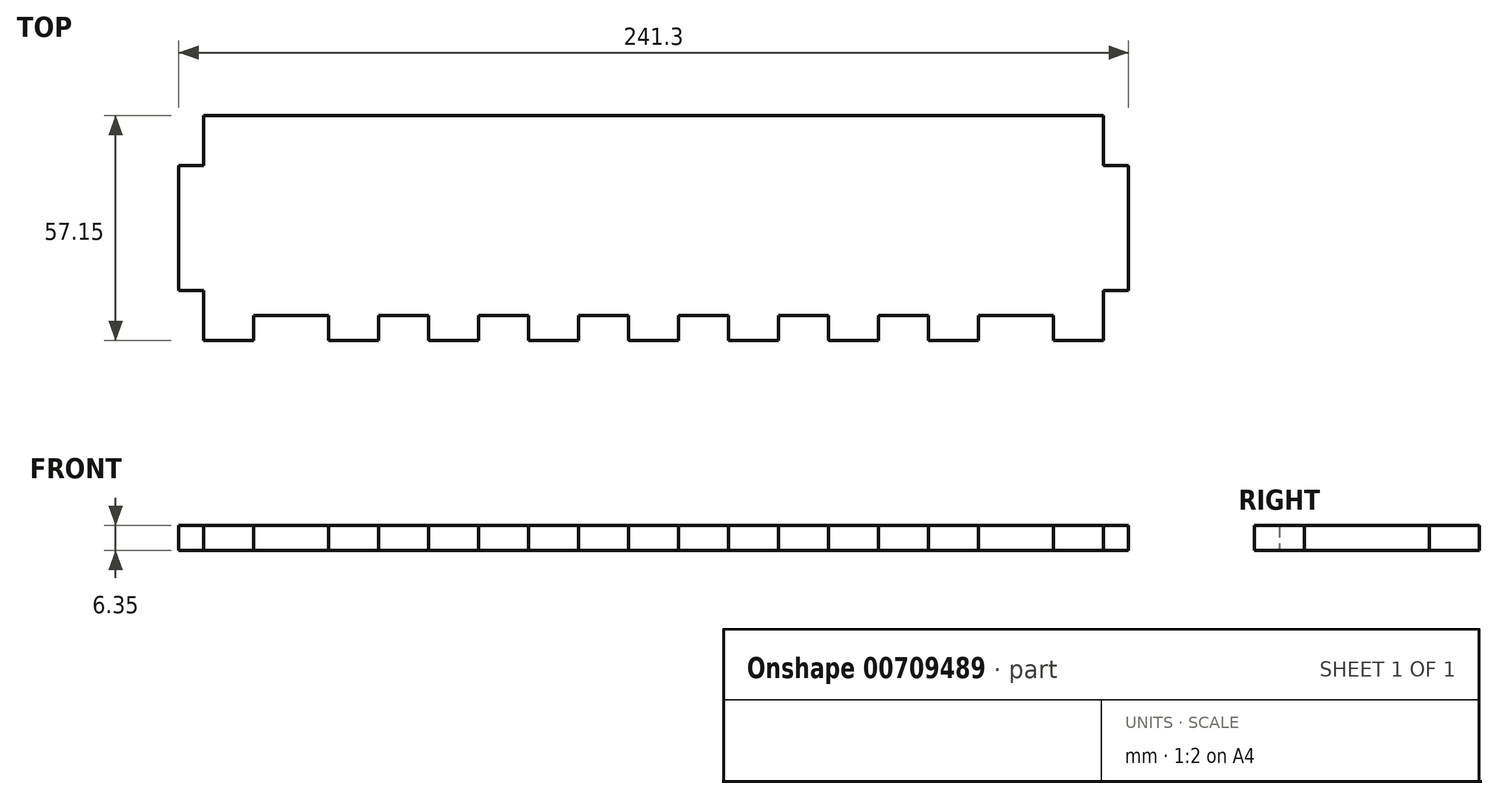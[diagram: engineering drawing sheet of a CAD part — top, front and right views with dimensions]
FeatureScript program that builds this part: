
annotation { "Feature Type Name" : "Feature", "Feature Type Description" : "" }
export const myFeature = defineFeature(function(context is Context, id is Id, definition is map)
    precondition{}
    {
        {
            var Q0;
            Q0=qCreatedBy(makeId("Top.planeOp"),FACE);
            var sketch = newSketch(context, id + "F0", { "sketchPlane" : qUnion([Q0])});
            skLineSegment(sketch, "E0.bottom", {"start": v(6.35, 0) * mm, "end": v(234.95, 0) * mm});
            skLineSegment(sketch, "E0.top", {"start": v(6.35, -57.15) * mm, "end": v(19.05, -57.15) * mm});
            skLineSegment(sketch, "E0.left", {"start": v(0, -12.7) * mm, "end": v(0, -44.45) * mm});
            skLineSegment(sketch, "E1", {"start": v(19.05, -57.15) * mm, "end": v(19.05, -50.8) * mm});
            skLineSegment(sketch, "E2", {"start": v(19.05, -50.8) * mm, "end": v(38.1, -50.8) * mm});
            skLineSegment(sketch, "E3", {"start": v(38.1, -50.8) * mm, "end": v(38.1, -57.15) * mm});
            skLineSegment(sketch, "E4", {"start": v(38.1, -57.15) * mm, "end": v(50.8, -57.15) * mm});
            skLineSegment(sketch, "E5", {"start": v(50.8, -57.15) * mm, "end": v(50.8, -50.8) * mm});
            skLineSegment(sketch, "E6", {"start": v(50.8, -50.8) * mm, "end": v(63.5, -50.8) * mm});
            skLineSegment(sketch, "E7", {"start": v(63.5, -50.8) * mm, "end": v(63.5, -57.15) * mm});
            skLineSegment(sketch, "E8", {"start": v(63.5, -57.15) * mm, "end": v(76.2, -57.15) * mm});
            skLineSegment(sketch, "E9", {"start": v(76.2, -57.15) * mm, "end": v(76.2, -50.8) * mm});
            skLineSegment(sketch, "E10", {"start": v(76.2, -50.8) * mm, "end": v(88.9, -50.8) * mm});
            skLineSegment(sketch, "E11", {"start": v(88.9, -50.8) * mm, "end": v(88.9, -57.15) * mm});
            skLineSegment(sketch, "E12", {"start": v(88.9, -57.15) * mm, "end": v(101.6, -57.15) * mm});
            skLineSegment(sketch, "E13", {"start": v(101.6, -57.15) * mm, "end": v(101.6, -50.8) * mm});
            skLineSegment(sketch, "E14", {"start": v(101.6, -50.8) * mm, "end": v(114.3, -50.8) * mm});
            skLineSegment(sketch, "E15", {"start": v(114.3, -50.8) * mm, "end": v(114.3, -57.15) * mm});
            skLineSegment(sketch, "E16.trimOffspring", {"start": v(114.3, -57.15) * mm, "end": v(127, -57.15) * mm});
            skLineSegment(sketch, "E17", {"start": v(127, -57.15) * mm, "end": v(127, -50.8) * mm});
            skLineSegment(sketch, "E18", {"start": v(127, -50.8) * mm, "end": v(139.7, -50.8) * mm});
            skLineSegment(sketch, "E19", {"start": v(139.7, -50.8) * mm, "end": v(139.7, -57.15) * mm});
            skLineSegment(sketch, "E20", {"start": v(139.7, -57.15) * mm, "end": v(152.4, -57.15) * mm});
            skLineSegment(sketch, "E21", {"start": v(152.4, -57.15) * mm, "end": v(152.4, -50.8) * mm});
            skLineSegment(sketch, "E22", {"start": v(152.4, -50.8) * mm, "end": v(165.1, -50.8) * mm});
            skLineSegment(sketch, "E23", {"start": v(165.1, -50.8) * mm, "end": v(165.1, -57.15) * mm});
            skLineSegment(sketch, "E24", {"start": v(165.1, -57.15) * mm, "end": v(177.8, -57.15) * mm});
            skLineSegment(sketch, "E25", {"start": v(177.8, -57.15) * mm, "end": v(177.8, -50.8) * mm});
            skLineSegment(sketch, "E26", {"start": v(177.8, -50.8) * mm, "end": v(190.5, -50.8) * mm});
            skLineSegment(sketch, "E27", {"start": v(190.5, -50.8) * mm, "end": v(190.5, -57.15) * mm});
            skLineSegment(sketch, "E28.trimOffspring", {"start": v(190.5, -57.15) * mm, "end": v(203.2, -57.15) * mm});
            skLineSegment(sketch, "E29", {"start": v(203.2, -57.15) * mm, "end": v(203.2, -50.8) * mm});
            skLineSegment(sketch, "E30", {"start": v(203.2, -50.8) * mm, "end": v(222.25, -50.8) * mm});
            skLineSegment(sketch, "E31", {"start": v(222.25, -50.8) * mm, "end": v(222.25, -57.15) * mm});
            skLineSegment(sketch, "E32.trimOffspring", {"start": v(222.25, -57.15) * mm, "end": v(234.95, -57.15) * mm});
            skLineSegment(sketch, "E33", {"start": v(6.35, -57.15) * mm, "end": v(6.35, -44.45) * mm});
            skLineSegment(sketch, "E34", {"start": v(6.35, -44.45) * mm, "end": v(0, -44.45) * mm});
            skLineSegment(sketch, "E35", {"start": v(0, -44.45) * mm, "end": v(0, -12.7) * mm});
            skLineSegment(sketch, "E36", {"start": v(0, -12.7) * mm, "end": v(6.35, -12.7) * mm});
            skLineSegment(sketch, "E37", {"start": v(6.35, -12.7) * mm, "end": v(6.35, 0) * mm});
            skPoint(sketch, "E38.orphan", {"position": v(0, -57.15) * mm});
            skPoint(sketch, "E39.orphan", {"position": v(0, 0) * mm});
            skLineSegment(sketch, "E40", {"start": v(120.65, -57.15) * mm, "end": v(120.65, -31.75) * mm, "construction": true});
            skLineSegment(sketch, "E41.MirrorCS", {"start": v(234.95, -12.7) * mm, "end": v(234.95, 0) * mm});
            skLineSegment(sketch, "E42.MirrorCS", {"start": v(241.3, -12.7) * mm, "end": v(234.95, -12.7) * mm});
            skLineSegment(sketch, "E43.MirrorCS", {"start": v(241.3, -44.45) * mm, "end": v(241.3, -12.7) * mm});
            skLineSegment(sketch, "E44.MirrorCS", {"start": v(234.95, -44.45) * mm, "end": v(241.3, -44.45) * mm});
            skLineSegment(sketch, "E45.MirrorCS", {"start": v(234.95, -57.15) * mm, "end": v(234.95, -44.45) * mm});
            skPoint(sketch, "E46.orphan", {"position": v(241.3, -57.15) * mm});
            skPoint(sketch, "E47.orphan", {"position": v(241.3, 0) * mm});
            skSolve(sketch);
        }
        {
            var Q0;
            Q0=makeQuery(id+"F0.imprint","IMPRINT",FACE,{"disambiguationData":[TD([[makeQuery(id+"F0.imprint","IMPRINT",EDGE,{"derivedFrom":sQuery(id+"F0.wireOp",EDGE,"E0.bottom")}),-1.0]])]});
            extrude(context, id + "F1", {"entities" : qUnion([Q0]), "depth" : 6.35 * mm, "offsetDistance" : 25.4 * mm});
        }
    });
